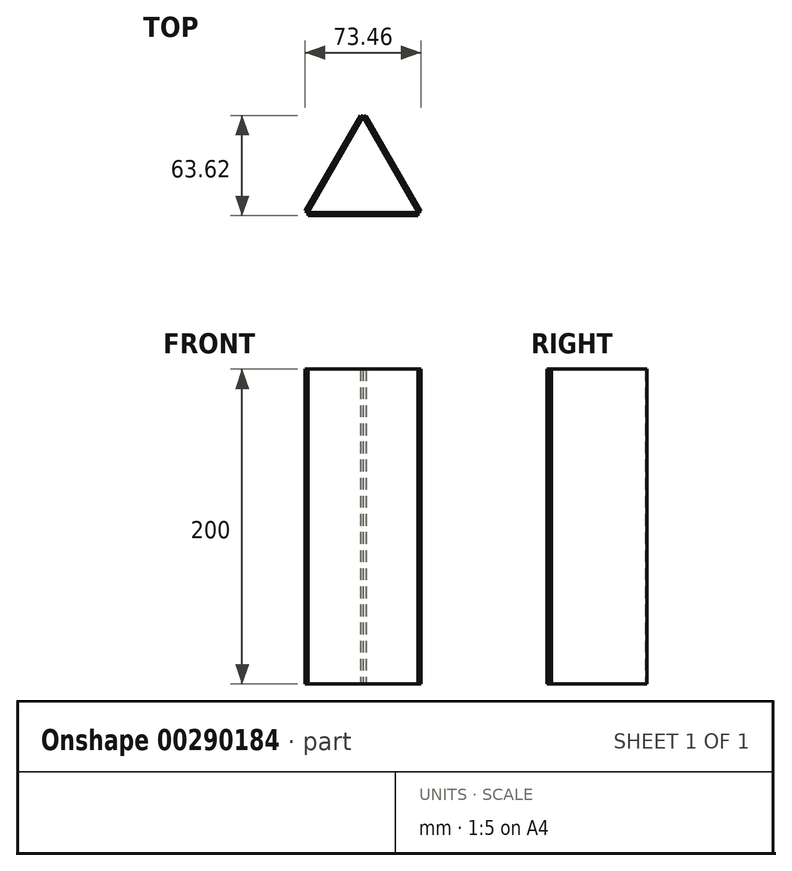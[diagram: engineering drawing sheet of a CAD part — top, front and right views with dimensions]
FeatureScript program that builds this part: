
annotation { "Feature Type Name" : "Feature", "Feature Type Description" : "" }
export const myFeature = defineFeature(function(context is Context, id is Id, definition is map)
    precondition{}
    {
        {
            var Q0;
            Q0=qCreatedBy(makeId("Top.planeOp"),FACE);
            var sketch = newSketch(context, id + "F0", { "sketchPlane" : qUnion([Q0])});
            skLineSegment(sketch, "E0", {"start": v(-35, 0) * mm, "end": v(35, 0) * mm});
            skLineSegment(sketch, "E1", {"start": v(-35, 2) * mm, "end": v(35, 2) * mm});
            skLineSegment(sketch, "E2", {"start": v(35, 2) * mm, "end": v(35, 0) * mm});
            skLineSegment(sketch, "E3", {"start": v(-35, 2) * mm, "end": v(-35, 0) * mm});
            skLineSegment(sketch, "E4", {"start": v(-35, 2) * mm, "end": v(0, 62.62) * mm});
            skLineSegment(sketch, "E5", {"start": v(-35, 2) * mm, "end": v(-36.73, 3) * mm});
            skLineSegment(sketch, "E6", {"start": v(-36.73, 3) * mm, "end": v(-1.73, 63.62) * mm});
            skLineSegment(sketch, "E7", {"start": v(-1.73, 63.62) * mm, "end": v(0, 62.62) * mm});
            skLineSegment(sketch, "E8.MirrorCS", {"start": v(35, 2) * mm, "end": v(0, 62.62) * mm});
            skLineSegment(sketch, "E9.MirrorCS", {"start": v(36.73, 3) * mm, "end": v(1.73, 63.62) * mm});
            skLineSegment(sketch, "E10.MirrorCS", {"start": v(1.73, 63.62) * mm, "end": v(0, 62.62) * mm});
            skLineSegment(sketch, "E11.MirrorCS", {"start": v(35, 2) * mm, "end": v(36.73, 3) * mm});
            skSolve(sketch);
        }
        {
            var Q0;
            Q0=makeQuery(id+"F0.imprint","IMPRINT",FACE,{"disambiguationData":[TD([[makeQuery(id+"F0.imprint","IMPRINT",EDGE,{"derivedFrom":sQuery(id+"F0.wireOp",EDGE,"E4")}),1.0]])]});
            var Q1;
            Q1=makeQuery(id+"F0.imprint","IMPRINT",FACE,{"disambiguationData":[TD([[makeQuery(id+"F0.imprint","IMPRINT",EDGE,{"derivedFrom":sQuery(id+"F0.wireOp",EDGE,"E0")}),1.0]])]});
            var Q2;
            Q2=makeQuery(id+"F0.imprint","IMPRINT",FACE,{"disambiguationData":[TD([[makeQuery(id+"F0.imprint","IMPRINT",EDGE,{"derivedFrom":sQuery(id+"F0.wireOp",EDGE,"E8.MirrorCS")}),-1.0]])]});
            extrude(context, id + "F1", {"entities" : qUnion([Q0, Q1, Q2]), "depth" : 200 * mm});
        }
    });
